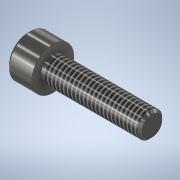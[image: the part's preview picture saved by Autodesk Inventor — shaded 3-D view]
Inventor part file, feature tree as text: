
AUTODESK INVENTOR PART (.ipt)
format: ipt  version: 2022 (Build 260153000, 153)  size: 160,256 bytes
history: native  units: mm
features: other x14, sketch x3, revolve x1, thread x1, hole x1, extrude x1
ambient origin geometry x8: Origin, YZ Plane, XZ Plane, XY Plane, X Axis, Y Axis, Z Axis, Center Point
bodies: Solid1 (feature_tree)
feature tree (21):
  revolve  "Revolution1"  [1 undecoded]
  thread  "Thread1"  [1 undecoded]
  hole  "Hole1"  [1 undecoded]
  extrude  "Extrusion1"  [1 undecoded]
  other  "bolt_XY"
  other  "bolt_YZ"
  other  "bolt_ZX"
  other  "bolt_X"
  other  "bolt_Y"
  other  "bolt_Z"
  other  "bolt_Center"
  other  "nut_XY"
  other  "nut_YZ"
  other  "nut_ZX"
  other  "nut_X"
  other  "nut_Y"
  other  "nut_Z"
  other  "nut_Center"
  sketch  "Sketch_1"  dims[d0=360.0deg d1=19.2mm d2=0.8mm]
  sketch  "Sketch2"  dims[d3=4.0mm d4=6.0mm d5=4.0mm d6=2.0mm d7=90.0deg d8=2.5mm d9=120.0deg d10=2.5mm d11=0.0mm]
  sketch  "Sketch_3"  dims[d12=0.0mm d13=0.0mm]
note: 4 required parameter values undecoded (feature->parameter linkage not recoverable at this tier; creation-order binding heuristic only, values carry confidence <= 0.55)